# Revit family: Calor White 1000
name_source: partatom
category: Generic Models
revit_build: Autodesk Revit 2018 (Build: 20190510_1515(x64)
units: mm (PartAtom-declared; Revit-internal decimal feet)

## family parameters
Always vertical = Yes
Can host rebar = No
Cut with Voids When Loaded = No
Host = Wall
Part Type = Normal
Room Calculation Point = No
Round Connector Dimension = Use Diameter
Shared = No

## types (4) — shared parameters
Placement height = 550 mm  [stored 1.80446 ft]
URL = http://masterwatt.nl

## per-type parameters (varying)
| type | Art. No. |
| Calor White 350 | 300 100 350 |
| Calor White 500 | 300 100 500 |
| Calor White 750 | 300 100 750 |
| Calor White 1000 | 300 101 000 |

note: column(s) folded — value = type name in every type: Model

type visibility flags: 4 boolean params named "<type name>" — each type sets only its own to Yes (folded from table)

note: [stored X ft] marks values corroborated as IEEE doubles in the binary element streams (Revit-internal decimal feet)

## geometry (parser evidence)
native form markers: Sweep x36
no freeform markers — native parametric forms only
